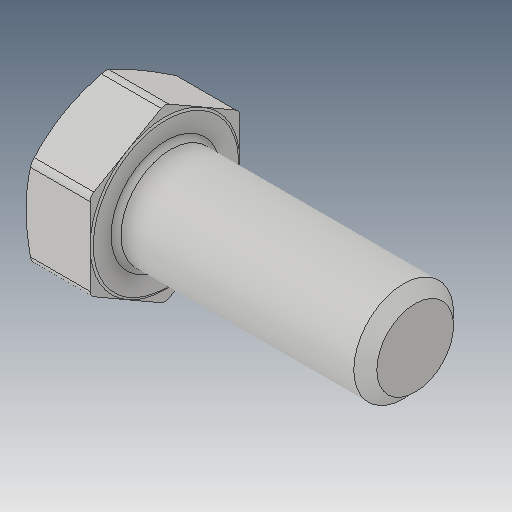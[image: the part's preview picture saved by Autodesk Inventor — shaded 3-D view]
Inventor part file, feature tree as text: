
AUTODESK INVENTOR PART (.ipt)
format: ipt  version: 2023.5 (Build 275446000, 446)  size: 174,592 bytes
history: native  units: in
note: dims shown in document units (in); Inventor stores cm internally (conversion verified against a paired STEP export)
features: fillet x1
ambient origin geometry x8: Origin, YZ Plane, XZ Plane, XY Plane, X Axis, Y Axis, Z Axis, Center Point
bodies: Solid1 (feature_tree)
feature tree (1):
  fillet  "Fillet4"  [1 undecoded]
note: 1 required parameter value undecoded (feature->parameter linkage not recoverable at this tier; creation-order binding heuristic only, values carry confidence <= 0.55)
